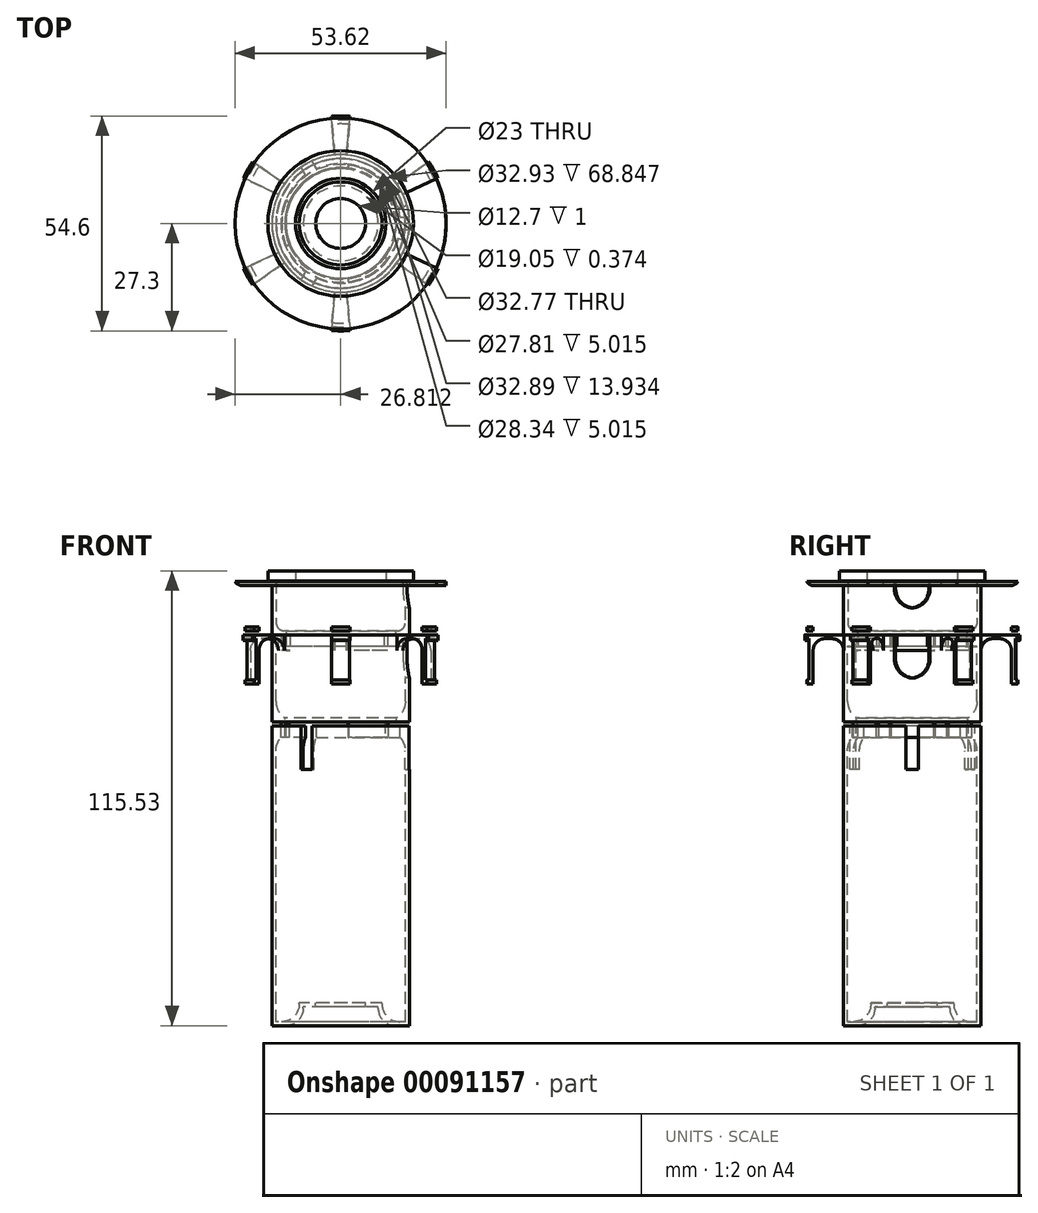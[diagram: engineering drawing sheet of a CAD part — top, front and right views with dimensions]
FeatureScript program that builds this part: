
annotation { "Feature Type Name" : "Feature", "Feature Type Description" : "" }
export const myFeature = defineFeature(function(context is Context, id is Id, definition is map)
    precondition{}
    {
        {
            var Q0;
            Q0=qCreatedBy(makeId("Front.planeOp"),FACE);
            var sketch = newSketch(context, id + "F0", { "sketchPlane" : qUnion([Q0])});
            skLineSegment(sketch, "E0", {"start": v(-75.46, 76.2) * mm, "end": v(-75.46, 0) * mm});
            skLineSegment(sketch, "E1", {"start": v(-75.46, 0) * mm, "end": v(-79, 0) * mm});
            skLineSegment(sketch, "E2", {"start": v(-83.4, 4.39) * mm, "end": v(-83.4, 4.76) * mm});
            skLineSegment(sketch, "E3", {"start": v(-83.4, 4.76) * mm, "end": v(-92.92, 4.76) * mm});
            skLineSegment(sketch, "E4.0", {"start": v(-82.4, 5.76) * mm, "end": v(-92.92, 5.76) * mm});
            skLineSegment(sketch, "E4.1", {"start": v(-82.4, 5.49) * mm, "end": v(-82.4, 5.76) * mm});
            skLineSegment(sketch, "E4.2", {"start": v(-76.46, 1) * mm, "end": v(-77.9, 1) * mm});
            skLineSegment(sketch, "E4.3", {"start": v(-76.46, 76.2) * mm, "end": v(-76.46, 1) * mm});
            skLineSegment(sketch, "E5", {"start": v(-76.46, 76.2) * mm, "end": v(-75.46, 76.2) * mm});
            skLineSegment(sketch, "E6", {"start": v(-92.92, 5.76) * mm, "end": v(-92.92, 4.76) * mm});
            skLineSegment(sketch, "E7.bottom", {"start": v(-86.57, 2.98) * mm, "end": v(-99.27, 2.98) * mm});
            skLineSegment(sketch, "E7.top", {"start": v(-86.57, 8.54) * mm, "end": v(-99.27, 8.54) * mm});
            skLineSegment(sketch, "E7.left", {"start": v(-86.57, 2.98) * mm, "end": v(-86.57, 8.54) * mm});
            skLineSegment(sketch, "E7.right", {"start": v(-99.27, 2.98) * mm, "end": v(-99.27, 8.54) * mm});
            skPoint(sketch, "E7.middle", {"position": v(-92.92, 5.76) * mm});
            skPoint(sketch, "E8.middle", {"position": v(-76.46, 76.2) * mm});
            skPoint(sketch, "E9.visualSharp", {"position": v(-82.4, 1) * mm});
            skArc(sketch, "E9.filletArc", {"start": v(-82.4, 5.49) * mm, "mid": v(-81.08, 2.31) * mm, "end": v(-77.9, 1) * mm});
            skPoint(sketch, "E10.visualSharp", {"position": v(-83.4, 0) * mm});
            skArc(sketch, "E10.filletArc", {"start": v(-83.4, 4.39) * mm, "mid": v(-82.1, 1.29) * mm, "end": v(-79, 0) * mm});
            skLineSegment(sketch, "E11", {"start": v(-92.92, 105.6) * mm, "end": v(-92.92, -5.85) * mm});
            skLineSegment(sketch, "E12.bottom", {"start": v(-77.75, 76.2) * mm, "end": v(-76.46, 76.2) * mm});
            skLineSegment(sketch, "E12.top", {"start": v(-77.75, 73.2) * mm, "end": v(-76.46, 73.2) * mm});
            skLineSegment(sketch, "E12.left", {"start": v(-77.75, 76.2) * mm, "end": v(-77.75, 73.2) * mm});
            skLineSegment(sketch, "E12.right", {"start": v(-76.46, 76.2) * mm, "end": v(-76.46, 73.2) * mm});
            skLineSegment(sketch, "E13", {"start": v(-75.46, 91.36) * mm, "end": v(-75.46, 98.33) * mm});
            skLineSegment(sketch, "E14", {"start": v(-75.46, 98.33) * mm, "end": v(-76.47, 98.33) * mm});
            skLineSegment(sketch, "E15", {"start": v(-76.47, 98.33) * mm, "end": v(-76.47, 78.2) * mm});
            skLineSegment(sketch, "E16", {"start": v(-76.47, 78.2) * mm, "end": v(-78.75, 78.2) * mm});
            skLineSegment(sketch, "E17", {"start": v(-78.75, 78.2) * mm, "end": v(-78.75, 73.19) * mm});
            skLineSegment(sketch, "E18", {"start": v(-78.75, 73.19) * mm, "end": v(-77.75, 73.2) * mm});
            skLineSegment(sketch, "E19", {"start": v(-77.75, 77.2) * mm, "end": v(-75.46, 77.2) * mm});
            skLineSegment(sketch, "E20", {"start": v(-75.46, 77.2) * mm, "end": v(-75.46, 91.36) * mm});
            skLineSegment(sketch, "E21", {"start": v(-77.75, 77.2) * mm, "end": v(-77.75, 73.2) * mm});
            skLineSegment(sketch, "E22.bottom", {"start": v(-77.75, 77.2) * mm, "end": v(-78.75, 77.2) * mm});
            skLineSegment(sketch, "E22.top", {"start": v(-77.75, 73.19) * mm, "end": v(-78.75, 73.19) * mm});
            skLineSegment(sketch, "E22.left", {"start": v(-77.75, 77.2) * mm, "end": v(-77.75, 73.19) * mm});
            skLineSegment(sketch, "E22.right", {"start": v(-78.75, 77.2) * mm, "end": v(-78.75, 73.19) * mm});
            skLineSegment(sketch, "E23.bottom", {"start": v(-76.47, 98.33) * mm, "end": v(-67.62, 98.33) * mm});
            skLineSegment(sketch, "E23.top", {"start": v(-76.47, 99.33) * mm, "end": v(-67.62, 99.33) * mm});
            skLineSegment(sketch, "E23.left", {"start": v(-76.47, 98.33) * mm, "end": v(-76.47, 99.33) * mm});
            skLineSegment(sketch, "E23.right", {"start": v(-67.62, 98.33) * mm, "end": v(-67.62, 99.33) * mm});
            skLineSegment(sketch, "E24.bottom", {"start": v(-67.62, 98.33) * mm, "end": v(-66.62, 98.33) * mm});
            skLineSegment(sketch, "E24.top", {"start": v(-67.62, 87.83) * mm, "end": v(-66.62, 87.83) * mm});
            skLineSegment(sketch, "E24.left", {"start": v(-67.62, 98.32) * mm, "end": v(-67.62, 87.83) * mm});
            skLineSegment(sketch, "E24.right", {"start": v(-66.62, 98.32) * mm, "end": v(-66.62, 87.83) * mm});
            skLineSegment(sketch, "E25.bottom", {"start": v(-67.62, 87.83) * mm, "end": v(-66.12, 87.83) * mm});
            skLineSegment(sketch, "E25.top", {"start": v(-67.62, 86.83) * mm, "end": v(-66.12, 86.83) * mm});
            skLineSegment(sketch, "E25.left", {"start": v(-67.62, 87.83) * mm, "end": v(-67.62, 86.83) * mm});
            skLineSegment(sketch, "E25.right", {"start": v(-66.12, 87.83) * mm, "end": v(-66.12, 86.83) * mm});
            skLineSegment(sketch, "E26.bottom", {"start": v(-67.62, 98.33) * mm, "end": v(-66.12, 98.33) * mm});
            skLineSegment(sketch, "E26.top", {"start": v(-67.62, 99.33) * mm, "end": v(-66.12, 99.33) * mm});
            skLineSegment(sketch, "E26.left", {"start": v(-67.62, 98.32) * mm, "end": v(-67.62, 99.33) * mm});
            skLineSegment(sketch, "E26.right", {"start": v(-66.12, 98.32) * mm, "end": v(-66.12, 99.33) * mm});
            skLineSegment(sketch, "E27", {"start": v(-67.62, 93.08) * mm, "end": v(-66.62, 93.08) * mm});
            skLineSegment(sketch, "E28.bottom", {"start": v(-66.12, 99.33) * mm, "end": v(-65.62, 99.33) * mm});
            skLineSegment(sketch, "E28.top", {"start": v(-66.12, 97.83) * mm, "end": v(-65.62, 97.83) * mm});
            skLineSegment(sketch, "E28.left", {"start": v(-66.12, 99.33) * mm, "end": v(-66.12, 97.83) * mm});
            skLineSegment(sketch, "E28.right", {"start": v(-65.62, 99.33) * mm, "end": v(-65.62, 97.83) * mm});
            skLineSegment(sketch, "E29", {"start": v(-75.46, 98.33) * mm, "end": v(-75.46, 99.33) * mm});
            skLineSegment(sketch, "E30.bottom", {"start": v(-76.47, 99.33) * mm, "end": v(-77.96, 99.33) * mm});
            skLineSegment(sketch, "E30.top", {"start": v(-76.47, 96.33) * mm, "end": v(-77.96, 96.33) * mm});
            skLineSegment(sketch, "E30.left", {"start": v(-76.47, 99.33) * mm, "end": v(-76.47, 96.33) * mm});
            skLineSegment(sketch, "E30.right", {"start": v(-77.96, 99.33) * mm, "end": v(-77.96, 96.33) * mm});
            skLineSegment(sketch, "E31", {"start": v(-76.47, 88.26) * mm, "end": v(-75.46, 88.26) * mm});
            skLineSegment(sketch, "E32.bottom", {"start": v(-74.42, 99.33) * mm, "end": v(-73.22, 99.33) * mm});
            skPoint(sketch, "E33.endSnap0", {"position": v(-77.96, 97.83) * mm});
            skLineSegment(sketch, "E34.bottom", {"start": v(-54.82, 105.48) * mm, "end": v(-54.82, 105.48) * mm});
            skLineSegment(sketch, "E34.top", {"start": v(-54.82, 105.48) * mm, "end": v(-54.82, 105.48) * mm});
            skLineSegment(sketch, "E34.left", {"start": v(-54.82, 105.48) * mm, "end": v(-54.82, 105.48) * mm});
            skLineSegment(sketch, "E34.right", {"start": v(-54.82, 105.48) * mm, "end": v(-54.82, 105.48) * mm});
            skLineSegment(sketch, "E35", {"start": v(-75.46, 111.83) * mm, "end": v(-75.46, 112.83) * mm});
            skLineSegment(sketch, "E36", {"start": v(-76.53, 111.83) * mm, "end": v(-76.53, 100.33) * mm});
            skLineSegment(sketch, "E37", {"start": v(-76.53, 100.33) * mm, "end": v(-79.01, 100.33) * mm});
            skLineSegment(sketch, "E38", {"start": v(-79.01, 100.33) * mm, "end": v(-79.01, 95.31) * mm});
            skLineSegment(sketch, "E39", {"start": v(-78.02, 99.33) * mm, "end": v(-75.46, 99.33) * mm});
            skLineSegment(sketch, "E40", {"start": v(-75.46, 99.33) * mm, "end": v(-75.46, 112.83) * mm});
            skLineSegment(sketch, "E41.top", {"start": v(-77.96, 95.31) * mm, "end": v(-79.01, 95.31) * mm});
            skLineSegment(sketch, "E41.left", {"start": v(-77.96, 99.33) * mm, "end": v(-77.96, 95.31) * mm});
            skLineSegment(sketch, "E41.right", {"start": v(-79.01, 99.33) * mm, "end": v(-79.01, 95.31) * mm});
            skLineSegment(sketch, "E42.bottom", {"start": v(-67.62, 101.33) * mm, "end": v(-66.12, 101.33) * mm});
            skLineSegment(sketch, "E42.top", {"start": v(-67.62, 100.33) * mm, "end": v(-66.12, 100.33) * mm});
            skLineSegment(sketch, "E42.left", {"start": v(-67.62, 101.33) * mm, "end": v(-67.62, 100.33) * mm});
            skLineSegment(sketch, "E42.right", {"start": v(-66.12, 101.33) * mm, "end": v(-66.12, 100.33) * mm});
            skLineSegment(sketch, "E43", {"start": v(-76.53, 111.83) * mm, "end": v(-67.62, 111.83) * mm});
            skLineSegment(sketch, "E44", {"start": v(-92.92, 105.6) * mm, "end": v(-92.92, 126.08) * mm});
            skLineSegment(sketch, "E45.bottom", {"start": v(-76.53, 111.83) * mm, "end": v(-66.1, 111.83) * mm});
            skLineSegment(sketch, "E45.top", {"start": v(-76.53, 112.83) * mm, "end": v(-66.1, 112.83) * mm});
            skLineSegment(sketch, "E45.left", {"start": v(-76.53, 111.83) * mm, "end": v(-76.53, 112.83) * mm});
            skLineSegment(sketch, "E45.right", {"start": v(-66.1, 111.83) * mm, "end": v(-66.1, 112.83) * mm});
            skLineSegment(sketch, "E46.bottom", {"start": v(-67.62, 111.83) * mm, "end": v(-66.62, 111.83) * mm});
            skLineSegment(sketch, "E46.top", {"start": v(-67.62, 101.33) * mm, "end": v(-66.62, 101.33) * mm});
            skLineSegment(sketch, "E46.left", {"start": v(-67.62, 111.83) * mm, "end": v(-67.62, 101.33) * mm});
            skLineSegment(sketch, "E46.right", {"start": v(-66.62, 111.83) * mm, "end": v(-66.62, 101.33) * mm});
            skLineSegment(sketch, "E47", {"start": v(-79.01, 99.33) * mm, "end": v(-77.96, 99.33) * mm});
            skLineSegment(sketch, "E48.bottom", {"start": v(-81.42, 113.03) * mm, "end": v(-74.42, 113.03) * mm});
            skLineSegment(sketch, "E48.top", {"start": v(-81.42, 115.53) * mm, "end": v(-74.42, 115.53) * mm});
            skLineSegment(sketch, "E48.left", {"start": v(-81.42, 113.03) * mm, "end": v(-81.42, 115.53) * mm});
            skLineSegment(sketch, "E48.right", {"start": v(-74.42, 113.03) * mm, "end": v(-74.42, 115.53) * mm});
            skLineSegment(sketch, "E49", {"start": v(-92.92, 121.65) * mm, "end": v(-56.65, 121.65) * mm});
            skLineSegment(sketch, "E50", {"start": v(-76.53, 106.08) * mm, "end": v(-75.46, 106.08) * mm});
            skSolve(sketch);
        }
        {
            var Q0;
            Q0=makeQuery(id+"F0.imprint","IMPRINT",FACE,{"disambiguationData":[TD([[makeQuery(id+"F0.imprint","IMPRINT",EDGE,{"derivedFrom":sQuery(id+"F0.wireOp",EDGE,"E0")}),-1.0]])]});
            var Q1;
            {var subQ5=sQuery(id+"F0.wireOp",EDGE,"E1");Q1=makeQuery(id+"F0.imprint","IMPRINT",FACE,{"disambiguationData":[TD([[makeQuery(id+"F0.imprint","IMPRINT",EDGE,{"derivedFrom":subQ5}),-1.0]])]});}
            var Q2;
            Q2=makeQuery(id+"F0.imprint","IMPRINT",FACE,{"disambiguationData":[TD([[makeQuery(id+"F0.imprint","IMPRINT",EDGE,{"derivedFrom":sQuery(id+"F0.wireOp",EDGE,"E12.bottom")}),-1.0]])]});
            var Q3;
            Q3=sQuery(id+"F0.wireOp",EDGE,"E6");
            revolve(context, id + "F1", {"entities" : qUnion([Q0, Q1, Q2]), "axis" : qUnion([Q3]), "revolveType" : RevolveType.FULL});
        }
        {
            var Q0;
            Q0=sQuery(id+"F0.wireOp",EDGE,"E1");
            var Q1;
            Q1=sQuery(id+"F0.wireOp",VERTEX,"E1.start");
            cPlane(context, id + "F2", {"entities" : qUnion([Q0, Q1]), "cplaneType" : CPlaneType.LINE_POINT, "offset" : 150 * mm, "width" : 150 * mm, "height" : 150 * mm});
        }
        {
            var Q0;
            Q0=qCreatedBy(id+"F2.planeOp",FACE);
            var sketch = newSketch(context, id + "F3", { "sketchPlane" : qUnion([Q0])});
            skLineSegment(sketch, "E51.bottom", {"start": v(-1.59, 65.09) * mm, "end": v(1.59, 65.09) * mm});
            skLineSegment(sketch, "E51.top", {"start": v(-1.59, 76.2) * mm, "end": v(1.59, 76.2) * mm});
            skLineSegment(sketch, "E51.left", {"start": v(-1.59, 65.09) * mm, "end": v(-1.59, 76.2) * mm});
            skLineSegment(sketch, "E51.right", {"start": v(1.59, 65.09) * mm, "end": v(1.59, 76.2) * mm});
            skPoint(sketch, "E51.middle", {"position": v(0, 70.64) * mm});
            skLineSegment(sketch, "E52.bottom", {"start": v(-3.65, 76.3) * mm, "end": v(3.11, 76.3) * mm});
            skLineSegment(sketch, "E52.top", {"start": v(-3.65, 68.35) * mm, "end": v(3.11, 68.35) * mm});
            skLineSegment(sketch, "E52.left", {"start": v(-3.65, 76.3) * mm, "end": v(-3.65, 68.35) * mm});
            skLineSegment(sketch, "E52.right", {"start": v(3.11, 76.3) * mm, "end": v(3.11, 68.35) * mm});
            skSolve(sketch);
        }
        {
            var Q0;
            Q0=makeQuery(id+"F3.imprint","IMPRINT",FACE,{"disambiguationData":[TD([[makeQuery(id+"F3.imprint","IMPRINT",EDGE,{"derivedFrom":sQuery(id+"F3.wireOp",EDGE,"E51.bottom")}),1.0]])]});
            var Q1;
            {var subQ0=sQuery(id+"F3.wireOp",EDGE,"E51.top");Q1=makeQuery(id+"F3.imprint","IMPRINT",FACE,{"disambiguationData":[TD([[makeQuery(id+"F3.imprint","IMPRINT",EDGE,{"derivedFrom":subQ0}),-1.0]])]});}
            extrude(context, id + "F4", {"entities" : qUnion([Q0, Q1]), "endBound" : BoundingType.SYMMETRIC, "depth" : 10 * mm});
        }
        {
            var Q0;
            Q0=makeQuery(id+"F4.opExtrude","SWEPT_BODY",BODY,{"disambiguationData":[OSD([sQuery(id+"F3.wireOp",EDGE,"E51.bottom"),sQuery(id+"F3.wireOp",EDGE,"E51.top"),sQuery(id+"F3.wireOp",EDGE,"E51.left"),sQuery(id+"F3.wireOp",EDGE,"E51.right")])]});
            var Q1;
            Q1=sQuery(id+"F0.wireOp",EDGE,"E6");
            circularPattern(context, id + "F5", {"operationType" : NewBodyOperationType.REMOVE, "entities" : qUnion([Q0]), "axis" : qUnion([Q1]), "angle" : 120 * degree, "instanceCount" : 3});
        }
        {
            var Q0;
            {var subQ0=sQuery(id+"F0.wireOp",EDGE,"E4.3");var subQ1=sQuery(id+"F0.wireOp",EDGE,"E12.top");Q0=makeQuery(id+"F5.boolean.opBoolean","SPLIT",EDGE,{"disambiguationData":[TD([makeQuery(id+"F4.opExtrude","SWEPT_FACE",FACE,{"disambiguationData":[OSD([sQuery(id+"F3.wireOp",EDGE,"E51.left")])]})])],"derivedFrom":makeQuery(id+"F1.opRevolve","SWEPT_EDGE",EDGE,{"disambiguationData":[OSD([subQ0,subQ1,sQuery(id+"F0.wireOp",EDGE,"E12.right")])]})});}
            var Q1;
            {var subQ0=sQuery(id+"F0.wireOp",EDGE,"E4.3");var subQ1=sQuery(id+"F0.wireOp",EDGE,"E12.top");Q1=makeQuery(id+"F5.boolean.opBoolean","SPLIT",EDGE,{"disambiguationData":[TD([makeQuery(id+"F4.opExtrude","SWEPT_FACE",FACE,{"disambiguationData":[OSD([sQuery(id+"F3.wireOp",EDGE,"E51.right")])]})])],"derivedFrom":makeQuery(id+"F1.opRevolve","SWEPT_EDGE",EDGE,{"disambiguationData":[OSD([subQ0,subQ1,sQuery(id+"F0.wireOp",EDGE,"E12.right")])]})});}
            var Q2;
            {var subQ0=sQuery(id+"F0.wireOp",EDGE,"E4.3");var subQ1=sQuery(id+"F0.wireOp",EDGE,"E12.top");Q2=makeQuery(id+"F5.boolean.opBoolean","SPLIT",EDGE,{"disambiguationData":[TD([makeQuery(id+"F5.opPattern","COPY",FACE,{"derivedFrom":makeQuery(id+"F4.opExtrude","SWEPT_FACE",FACE,{"disambiguationData":[OSD([sQuery(id+"F3.wireOp",EDGE,"E51.right")])]}),"instanceName":"1"})])],"derivedFrom":makeQuery(id+"F1.opRevolve","SWEPT_EDGE",EDGE,{"disambiguationData":[OSD([subQ0,subQ1,sQuery(id+"F0.wireOp",EDGE,"E12.right")])]})});}
            fillet(context, id + "F6", {"entities" : qUnion([Q0, Q1, Q2]), "radius" : 5 * mm, "tangentPropagation" : true, "allowEdgeOverflow" : false});
        }
        {
            var Q0;
            Q0=makeQuery(id+"F0.imprint","IMPRINT",FACE,{"disambiguationData":[TD([[makeQuery(id+"F0.imprint","IMPRINT",EDGE,{"derivedFrom":sQuery(id+"F0.wireOp",EDGE,"E13")}),1.0]])]});
            var Q1;
            {var subQ3=sQuery(id+"F0.wireOp",EDGE,"E18");Q1=makeQuery(id+"F0.imprint","IMPRINT",FACE,{"disambiguationData":[TD([[makeQuery(id+"F0.imprint","IMPRINT",EDGE,{"derivedFrom":subQ3}),1.0]])]});}
            var Q2;
            Q2=makeQuery(id+"F0.imprint","IMPRINT",FACE,{"disambiguationData":[TD([[makeQuery(id+"F0.imprint","IMPRINT",EDGE,{"derivedFrom":sQuery(id+"F0.wireOp",EDGE,"E23.top")}),-1.0]])]});
            var Q3;
            {var subQ1=sQuery(id+"F0.wireOp",EDGE,"E26.top");Q3=makeQuery(id+"F0.imprint","IMPRINT",FACE,{"disambiguationData":[TD([[makeQuery(id+"F0.imprint","IMPRINT",EDGE,{"derivedFrom":subQ1}),-1.0]])]});}
            var Q4;
            {var subQ3=sQuery(id+"F0.wireOp",EDGE,"E28.bottom");Q4=makeQuery(id+"F0.imprint","IMPRINT",FACE,{"disambiguationData":[TD([[makeQuery(id+"F0.imprint","IMPRINT",EDGE,{"derivedFrom":subQ3}),-1.0]])]});}
            var Q5;
            {var subQ3=sQuery(id+"F0.wireOp",EDGE,"E27");Q5=makeQuery(id+"F0.imprint","IMPRINT",FACE,{"disambiguationData":[TD([[makeQuery(id+"F0.imprint","IMPRINT",EDGE,{"derivedFrom":subQ3}),1.0]])]});}
            var Q6;
            {var subQ3=sQuery(id+"F0.wireOp",EDGE,"E27");Q6=makeQuery(id+"F0.imprint","IMPRINT",FACE,{"disambiguationData":[TD([[makeQuery(id+"F0.imprint","IMPRINT",EDGE,{"derivedFrom":subQ3}),-1.0]])]});}
            var Q7;
            Q7=makeQuery(id+"F0.imprint","IMPRINT",FACE,{"disambiguationData":[TD([[makeQuery(id+"F0.imprint","IMPRINT",EDGE,{"derivedFrom":sQuery(id+"F0.wireOp",EDGE,"E25.top")}),1.0]])]});
            var Q8;
            {var subQ3=sQuery(id+"F0.wireOp",EDGE,"E30.bottom");Q8=makeQuery(id+"F0.imprint","IMPRINT",FACE,{"disambiguationData":[TD([[makeQuery(id+"F0.imprint","IMPRINT",EDGE,{"derivedFrom":subQ3}),1.0]])]});}
            var Q9;
            {var subQ1=sQuery(id+"F0.wireOp",EDGE,"E16");Q9=makeQuery(id+"F0.imprint","IMPRINT",FACE,{"disambiguationData":[TD([[makeQuery(id+"F0.imprint","IMPRINT",EDGE,{"derivedFrom":subQ1}),1.0]])]});}
            var Q10;
            {var subQ0=sQuery(id+"F0.wireOp",EDGE,"E29");Q10=makeQuery(id+"F0.imprint","IMPRINT",FACE,{"disambiguationData":[TD([[makeQuery(id+"F0.imprint","IMPRINT",EDGE,{"derivedFrom":subQ0}),1.0]])]});}
            var Q11;
            Q11=makeQuery(id+"F0.imprint","IMPRINT",FACE,{"disambiguationData":[TD([[makeQuery(id+"F0.imprint","IMPRINT",EDGE,{"derivedFrom":sQuery(id+"F0.wireOp",EDGE,"E32.bottom")}),1.0]])]});
            var Q12;
            Q12=sQuery(id+"F0.wireOp",EDGE,"E11");
            revolve(context, id + "F7", {"entities" : qUnion([Q0, Q1, Q2, Q3, Q4, Q5, Q6, Q7, Q8, Q9, Q10, Q11]), "axis" : qUnion([Q12]), "revolveType" : RevolveType.FULL});
        }
        {
            var Q0;
            {var subQ3=sQuery(id+"F0.wireOp",EDGE,"E18");Q0=makeQuery(id+"F0.imprint","IMPRINT",FACE,{"disambiguationData":[TD([[makeQuery(id+"F0.imprint","IMPRINT",EDGE,{"derivedFrom":subQ3}),1.0]])]});}
            var Q1;
            Q1=sQuery(id+"F0.wireOp",EDGE,"E11");
            revolve(context, id + "F8", {"entities" : qUnion([Q0]), "axis" : qUnion([Q1]), "revolveType" : RevolveType.SYMMETRIC, "angle" : 75 * degree});
        }
        {
            var Q0;
            Q0=makeQuery(id+"F8.opRevolve","SWEPT_BODY",BODY,{"disambiguationData":[OSD([sQuery(id+"F0.wireOp",EDGE,"E18"),sQuery(id+"F0.wireOp",EDGE,"E22.bottom"),sQuery(id+"F0.wireOp",EDGE,"E22.left"),sQuery(id+"F0.wireOp",EDGE,"E22.right")])]});
            var Q1;
            Q1=sQuery(id+"F0.wireOp",EDGE,"E11");
            circularPattern(context, id + "F9", {"operationType" : NewBodyOperationType.REMOVE, "entities" : qUnion([Q0]), "axis" : qUnion([Q1]), "angle" : 120 * degree, "instanceCount" : 3});
        }
        {
            var Q0;
            Q0=makeQuery(id+"F7.opRevolve","SWEPT_EDGE",EDGE,{"disambiguationData":[OSD([sQuery(id+"F0.wireOp",EDGE,"E15"),sQuery(id+"F0.wireOp",EDGE,"E16")])]});
            fillet(context, id + "F10", {"entities" : qUnion([Q0]), "radius" : 5 * mm, "tangentPropagation" : true, "allowEdgeOverflow" : false});
        }
        {
            var Q0;
            {var subQ2=sQuery(id+"F0.wireOp",EDGE,"E26.left");Q0=makeQuery(id+"F0.imprint","IMPRINT",FACE,{"disambiguationData":[TD([[makeQuery(id+"F0.imprint","IMPRINT",EDGE,{"derivedFrom":subQ2}),1.0]])]});}
            var Q1;
            {var subQ1=sQuery(id+"F0.wireOp",EDGE,"E26.top");Q1=makeQuery(id+"F0.imprint","IMPRINT",FACE,{"disambiguationData":[TD([[makeQuery(id+"F0.imprint","IMPRINT",EDGE,{"derivedFrom":subQ1}),-1.0]])]});}
            var Q2;
            {var subQ3=sQuery(id+"F0.wireOp",EDGE,"E28.bottom");Q2=makeQuery(id+"F0.imprint","IMPRINT",FACE,{"disambiguationData":[TD([[makeQuery(id+"F0.imprint","IMPRINT",EDGE,{"derivedFrom":subQ3}),-1.0]])]});}
            var Q3;
            {var subQ3=sQuery(id+"F0.wireOp",EDGE,"E27");Q3=makeQuery(id+"F0.imprint","IMPRINT",FACE,{"disambiguationData":[TD([[makeQuery(id+"F0.imprint","IMPRINT",EDGE,{"derivedFrom":subQ3}),1.0]])]});}
            var Q4;
            {var subQ3=sQuery(id+"F0.wireOp",EDGE,"E27");Q4=makeQuery(id+"F0.imprint","IMPRINT",FACE,{"disambiguationData":[TD([[makeQuery(id+"F0.imprint","IMPRINT",EDGE,{"derivedFrom":subQ3}),-1.0]])]});}
            var Q5;
            Q5=makeQuery(id+"F0.imprint","IMPRINT",FACE,{"disambiguationData":[TD([[makeQuery(id+"F0.imprint","IMPRINT",EDGE,{"derivedFrom":sQuery(id+"F0.wireOp",EDGE,"E25.top")}),1.0]])]});
            var Q6;
            Q6=makeQuery(id+"F0.imprint","IMPRINT",FACE,{"disambiguationData":[TD([[makeQuery(id+"F0.imprint","IMPRINT",EDGE,{"derivedFrom":sQuery(id+"F0.wireOp",EDGE,"E32.bottom")}),1.0]])]});
            var Q7;
            Q7=sQuery(id+"F0.wireOp",EDGE,"E11");
            revolve(context, id + "F11", {"entities" : qUnion([Q0, Q1, Q2, Q3, Q4, Q5, Q6]), "axis" : qUnion([Q7]), "revolveType" : RevolveType.SYMMETRIC, "angle" : 50 * degree});
        }
        {
            var Q0;
            Q0=makeQuery(id+"F11.opRevolve","SWEPT_BODY",BODY,{"disambiguationData":[OSD([sQuery(id+"F0.wireOp",EDGE,"E23.bottom"),sQuery(id+"F0.wireOp",EDGE,"E23.top"),sQuery(id+"F0.wireOp",EDGE,"E24.left"),sQuery(id+"F0.wireOp",EDGE,"E24.right"),sQuery(id+"F0.wireOp",EDGE,"E25.bottom"),sQuery(id+"F0.wireOp",EDGE,"E25.top"),sQuery(id+"F0.wireOp",EDGE,"E25.left"),sQuery(id+"F0.wireOp",EDGE,"E25.right"),sQuery(id+"F0.wireOp",EDGE,"E26.bottom"),sQuery(id+"F0.wireOp",EDGE,"E26.top"),sQuery(id+"F0.wireOp",EDGE,"E28.bottom"),sQuery(id+"F0.wireOp",EDGE,"E28.top"),sQuery(id+"F0.wireOp",EDGE,"E28.left"),sQuery(id+"F0.wireOp",EDGE,"E28.right"),sQuery(id+"F0.wireOp",EDGE,"E29")])]});
            var Q1;
            Q1=sQuery(id+"F0.wireOp",EDGE,"E11");
            circularPattern(context, id + "F12", {"operationType" : NewBodyOperationType.REMOVE, "entities" : qUnion([Q0]), "axis" : qUnion([Q1]), "angle" : 60 * degree, "instanceCount" : 6});
        }
        {
            var Q0;
            {var subQ1=sQuery(id+"F0.wireOp",EDGE,"E13");Q0=makeQuery(id+"F0.imprint","IMPRINT",FACE,{"disambiguationData":[TD([[makeQuery(id+"F0.imprint","IMPRINT",EDGE,{"derivedFrom":subQ1}),1.0]])]});}
            var Q1;
            {var subQ3=sQuery(id+"F0.wireOp",EDGE,"E30.bottom");Q1=makeQuery(id+"F0.imprint","IMPRINT",FACE,{"disambiguationData":[TD([[makeQuery(id+"F0.imprint","IMPRINT",EDGE,{"derivedFrom":subQ3}),1.0]])]});}
            var Q2;
            {var subQ0=sQuery(id+"F0.wireOp",EDGE,"E29");Q2=makeQuery(id+"F0.imprint","IMPRINT",FACE,{"disambiguationData":[TD([[makeQuery(id+"F0.imprint","IMPRINT",EDGE,{"derivedFrom":subQ0}),1.0]])]});}
            var Q3;
            Q3=sQuery(id+"F0.wireOp",EDGE,"E11");
            revolve(context, id + "F13", {"operationType" : NewBodyOperationType.REMOVE, "entities" : qUnion([Q0, Q1, Q2]), "axis" : qUnion([Q3]), "revolveType" : RevolveType.SYMMETRIC, "oppositeDirection" : true, "angle" : 30 * degree});
        }
        {
            var Q0;
            Q0=makeQuery(id+"F13.boolean.opBoolean","COPY",EDGE,{"derivedFrom":makeQuery(id+"F13.opRevolve","CAP_EDGE",EDGE,{"disambiguationData":[OSD([sQuery(id+"F0.wireOp",EDGE,"E31")])],"isStart":false})});
            var Q1;
            Q1=makeQuery(id+"F13.boolean.opBoolean","COPY",EDGE,{"derivedFrom":makeQuery(id+"F13.opRevolve","CAP_EDGE",EDGE,{"disambiguationData":[OSD([sQuery(id+"F0.wireOp",EDGE,"E31")])],"isStart":true})});
            fillet(context, id + "F14", {"entities" : qUnion([Q0, Q1]), "radius" : 5 * mm, "tangentPropagation" : true, "allowEdgeOverflow" : false});
        }
        {
            var Q0;
            Q0=makeQuery(id+"F13.boolean.opBoolean","SPLIT",EDGE,{"disambiguationData":[OD(1.0)],"derivedFrom":makeQuery(id+"F7.opRevolve","SWEPT_EDGE",EDGE,{"disambiguationData":[OSD([sQuery(id+"F0.wireOp",EDGE,"E13"),sQuery(id+"F0.wireOp",EDGE,"E23.bottom"),sQuery(id+"F0.wireOp",EDGE,"E29")])]})});
            var Q1;
            Q1=makeQuery(id+"F7.opRevolve","SWEPT_EDGE",EDGE,{"disambiguationData":[OSD([sQuery(id+"F0.wireOp",EDGE,"E23.bottom"),sQuery(id+"F0.wireOp",EDGE,"E24.left"),sQuery(id+"F0.wireOp",EDGE,"E26.bottom"),sQuery(id+"F0.wireOp",EDGE,"E26.left")])]});
            fillet(context, id + "F15", {"entities" : qUnion([Q0, Q1]), "radius" : 3 * mm, "tangentPropagation" : true, "allowEdgeOverflow" : false});
        }
        {
            var Q0;
            Q0=makeQuery(id+"F0.imprint","IMPRINT",FACE,{"disambiguationData":[TD([[makeQuery(id+"F0.imprint","IMPRINT",EDGE,{"derivedFrom":sQuery(id+"F0.wireOp",EDGE,"E42.bottom")}),-1.0]])]});
            var Q1;
            Q1=makeQuery(id+"F0.imprint","IMPRINT",FACE,{"disambiguationData":[TD([[makeQuery(id+"F0.imprint","IMPRINT",EDGE,{"derivedFrom":sQuery(id+"F0.wireOp",EDGE,"E46.bottom")}),-1.0]])]});
            var Q2;
            {var subQ3=sQuery(id+"F0.wireOp",EDGE,"E45.right");Q2=makeQuery(id+"F0.imprint","IMPRINT",FACE,{"disambiguationData":[TD([[makeQuery(id+"F0.imprint","IMPRINT",EDGE,{"derivedFrom":subQ3}),1.0]])]});}
            var Q3;
            {var subQ5=sQuery(id+"F0.wireOp",EDGE,"E45.left");Q3=makeQuery(id+"F0.imprint","IMPRINT",FACE,{"disambiguationData":[TD([[makeQuery(id+"F0.imprint","IMPRINT",EDGE,{"derivedFrom":subQ5}),-1.0]])]});}
            var Q4;
            {var subQ6=sQuery(id+"F0.wireOp",EDGE,"E36");Q4=makeQuery(id+"F0.imprint","IMPRINT",FACE,{"disambiguationData":[TD([[makeQuery(id+"F0.imprint","IMPRINT",EDGE,{"derivedFrom":subQ6}),1.0]])]});}
            var Q5;
            {var subQ3=sQuery(id+"F0.wireOp",EDGE,"E41.top");Q5=makeQuery(id+"F0.imprint","IMPRINT",FACE,{"disambiguationData":[TD([[makeQuery(id+"F0.imprint","IMPRINT",EDGE,{"derivedFrom":subQ3}),-1.0]])]});}
            var Q6;
            {var subQ7=sQuery(id+"F0.wireOp",EDGE,"E37");Q6=makeQuery(id+"F0.imprint","IMPRINT",FACE,{"disambiguationData":[TD([[makeQuery(id+"F0.imprint","IMPRINT",EDGE,{"derivedFrom":subQ7}),1.0]])]});}
            var Q7;
            Q7=sQuery(id+"F0.wireOp",EDGE,"E44");
            revolve(context, id + "F16", {"entities" : qUnion([Q0, Q1, Q2, Q3, Q4, Q5, Q6]), "axis" : qUnion([Q7]), "revolveType" : RevolveType.FULL});
        }
        {
            var Q0;
            {var subQ3=sQuery(id+"F0.wireOp",EDGE,"E41.top");Q0=makeQuery(id+"F0.imprint","IMPRINT",FACE,{"disambiguationData":[TD([[makeQuery(id+"F0.imprint","IMPRINT",EDGE,{"derivedFrom":subQ3}),-1.0]])]});}
            var Q1;
            Q1=sQuery(id+"F0.wireOp",EDGE,"E11");
            revolve(context, id + "F17", {"entities" : qUnion([Q0]), "axis" : qUnion([Q1]), "revolveType" : RevolveType.SYMMETRIC, "angle" : 75 * degree});
        }
        {
            var Q0;
            Q0=makeQuery(id+"F17.opRevolve","SWEPT_BODY",BODY,{"disambiguationData":[OSD([sQuery(id+"F0.wireOp",EDGE,"E41.top"),sQuery(id+"F0.wireOp",EDGE,"E41.left"),sQuery(id+"F0.wireOp",EDGE,"E41.right"),sQuery(id+"F0.wireOp",EDGE,"E47")])]});
            var Q1;
            Q1=sQuery(id+"F0.wireOp",EDGE,"E11");
            circularPattern(context, id + "F18", {"operationType" : NewBodyOperationType.REMOVE, "entities" : qUnion([Q0]), "axis" : qUnion([Q1]), "angle" : 120 * degree, "instanceCount" : 3});
        }
        {
            var Q0;
            Q0=makeQuery(id+"F16.opRevolve","SWEPT_EDGE",EDGE,{"disambiguationData":[OSD([sQuery(id+"F0.wireOp",EDGE,"E36"),sQuery(id+"F0.wireOp",EDGE,"E37")])]});
            fillet(context, id + "F19", {"entities" : qUnion([Q0]), "radius" : 2 * mm, "tangentPropagation" : true, "allowEdgeOverflow" : false});
        }
        {
            var Q0;
            Q0=makeQuery(id+"F0.imprint","IMPRINT",FACE,{"disambiguationData":[TD([[makeQuery(id+"F0.imprint","IMPRINT",EDGE,{"derivedFrom":sQuery(id+"F0.wireOp",EDGE,"E42.bottom")}),-1.0]])]});
            var Q1;
            Q1=makeQuery(id+"F0.imprint","IMPRINT",FACE,{"disambiguationData":[TD([[makeQuery(id+"F0.imprint","IMPRINT",EDGE,{"derivedFrom":sQuery(id+"F0.wireOp",EDGE,"E46.bottom")}),-1.0]])]});
            var Q2;
            {var subQ3=sQuery(id+"F0.wireOp",EDGE,"E45.right");Q2=makeQuery(id+"F0.imprint","IMPRINT",FACE,{"disambiguationData":[TD([[makeQuery(id+"F0.imprint","IMPRINT",EDGE,{"derivedFrom":subQ3}),1.0]])]});}
            var Q3;
            Q3=sQuery(id+"F0.wireOp",EDGE,"E44");
            revolve(context, id + "F20", {"entities" : qUnion([Q0, Q1, Q2]), "axis" : qUnion([Q3]), "revolveType" : RevolveType.SYMMETRIC, "angle" : 50 * degree});
        }
        {
            var Q0;
            Q0=makeQuery(id+"F20.opRevolve","SWEPT_BODY",BODY,{"disambiguationData":[OSD([sQuery(id+"F0.wireOp",EDGE,"E42.bottom"),sQuery(id+"F0.wireOp",EDGE,"E42.top"),sQuery(id+"F0.wireOp",EDGE,"E42.left"),sQuery(id+"F0.wireOp",EDGE,"E42.right"),sQuery(id+"F0.wireOp",EDGE,"E45.bottom"),sQuery(id+"F0.wireOp",EDGE,"E45.top"),sQuery(id+"F0.wireOp",EDGE,"E45.left"),sQuery(id+"F0.wireOp",EDGE,"E45.right"),sQuery(id+"F0.wireOp",EDGE,"E46.left"),sQuery(id+"F0.wireOp",EDGE,"E46.right")])]});
            var Q1;
            Q1=sQuery(id+"F0.wireOp",EDGE,"E44");
            circularPattern(context, id + "F21", {"operationType" : NewBodyOperationType.REMOVE, "entities" : qUnion([Q0]), "axis" : qUnion([Q1]), "angle" : 60 * degree, "instanceCount" : 6});
        }
        {
            var Q0;
            {var subQ0=sQuery(id+"F0.wireOp",EDGE,"E46.left");var subQ1=sQuery(id+"F0.wireOp",EDGE,"E45.bottom");var subQ2=sQuery(id+"F0.wireOp",EDGE,"E40");var subQ3=makeQuery(id+"F0.imprint","INTERSECT",VERTEX,{"derivedFrom":[subQ2,subQ1]});var subQ4=makeQuery(id+"F0.imprint","IMPRINT",EDGE,{"disambiguationData":[TD([[subQ3,-1.0]])],"derivedFrom":subQ1});var subQ5=sQuery(id+"F0.wireOp",EDGE,"E45.left");var subQ6=makeQuery(id+"F20.opRevolve","SWEPT_FACE",FACE,{"disambiguationData":[OSD([subQ1]),TDD([makeQuery(id+"F0.imprint","IMPRINT",EDGE,{"disambiguationData":[TD([[subQ3,1.0]])],"derivedFrom":subQ1}),subQ4])]});var subQ7=sQuery(id+"F0.wireOp",EDGE,"E46.right");var subQ8=sQuery(id+"F0.wireOp",EDGE,"E45.right");var subQ9=sQuery(id+"F0.wireOp",EDGE,"E45.top");var subQ10=sQuery(id+"F0.wireOp",EDGE,"E42.right");var subQ11=sQuery(id+"F0.wireOp",EDGE,"E42.left");var subQ12=sQuery(id+"F0.wireOp",EDGE,"E42.top");var subQ13=sQuery(id+"F0.wireOp",EDGE,"E42.bottom");Q0=makeQuery(id+"F21.boolean.opBoolean","SPLIT",EDGE,{"disambiguationData":[TD([makeQuery(id+"F16.opRevolve","SWEPT_FACE",FACE,{"disambiguationData":[OSD([subQ2])]}),makeQuery(id+"F16.opRevolve","SWEPT_FACE",FACE,{"disambiguationData":[OSD([subQ1]),TDD([subQ4])]}),makeQuery(id+"F21.opPattern","COPY",FACE,{"derivedFrom":makeQuery(id+"F20.opRevolve","CAP_FACE",FACE,{"disambiguationData":[OSD([subQ13,subQ12,subQ11,subQ10,subQ1,subQ9,subQ5,subQ8,subQ0,subQ7])],"isStart":false}),"instanceName":"3"}),makeQuery(id+"F21.opPattern","COPY",FACE,{"derivedFrom":subQ6,"instanceName":"3"}),makeQuery(id+"F21.opPattern","COPY",FACE,{"derivedFrom":makeQuery(id+"F20.opRevolve","CAP_FACE",FACE,{"disambiguationData":[OSD([subQ13,subQ12,subQ11,subQ10,subQ1,subQ9,subQ5,subQ8,subQ0,subQ7])],"isStart":true}),"instanceName":"4"}),makeQuery(id+"F21.opPattern","COPY",FACE,{"derivedFrom":subQ6,"instanceName":"4"})])],"derivedFrom":makeQuery(id+"F16.opRevolve","SWEPT_EDGE",EDGE,{"disambiguationData":[OSD([subQ2,subQ1])]})});}
            var Q1;
            {var subQ0=sQuery(id+"F0.wireOp",EDGE,"E46.left");var subQ1=sQuery(id+"F0.wireOp",EDGE,"E42.left");var subQ2=sQuery(id+"F0.wireOp",EDGE,"E46.bottom");var subQ3=sQuery(id+"F0.wireOp",EDGE,"E45.bottom");var subQ4=sQuery(id+"F0.wireOp",EDGE,"E46.right");var subQ5=sQuery(id+"F0.wireOp",EDGE,"E45.right");var subQ6=sQuery(id+"F0.wireOp",EDGE,"E45.left");var subQ7=sQuery(id+"F0.wireOp",EDGE,"E45.top");var subQ8=sQuery(id+"F0.wireOp",EDGE,"E42.right");var subQ9=sQuery(id+"F0.wireOp",EDGE,"E42.top");var subQ10=sQuery(id+"F0.wireOp",EDGE,"E42.bottom");Q1=makeQuery(id+"F21.boolean.opBoolean","SPLIT",EDGE,{"disambiguationData":[TD([makeQuery(id+"F21.opPattern","COPY",FACE,{"derivedFrom":makeQuery(id+"F20.opRevolve","CAP_FACE",FACE,{"disambiguationData":[OSD([subQ10,subQ9,subQ1,subQ8,subQ3,subQ7,subQ6,subQ5,subQ0,subQ4])],"isStart":false}),"instanceName":"4"})])],"derivedFrom":makeQuery(id+"F16.opRevolve","SWEPT_EDGE",EDGE,{"disambiguationData":[OSD([subQ3,subQ2,subQ0])]})});}
            var Q2;
            {var subQ0=sQuery(id+"F0.wireOp",EDGE,"E46.right");var subQ1=sQuery(id+"F0.wireOp",EDGE,"E46.left");var subQ2=sQuery(id+"F0.wireOp",EDGE,"E45.right");var subQ3=sQuery(id+"F0.wireOp",EDGE,"E45.left");var subQ4=sQuery(id+"F0.wireOp",EDGE,"E45.top");var subQ5=sQuery(id+"F0.wireOp",EDGE,"E45.bottom");var subQ6=sQuery(id+"F0.wireOp",EDGE,"E42.right");var subQ7=sQuery(id+"F0.wireOp",EDGE,"E42.left");var subQ8=sQuery(id+"F0.wireOp",EDGE,"E42.top");var subQ9=sQuery(id+"F0.wireOp",EDGE,"E42.bottom");var subQ10=sQuery(id+"F0.wireOp",EDGE,"E40");var subQ11=makeQuery(id+"F0.imprint","INTERSECT",VERTEX,{"derivedFrom":[subQ10,subQ5]});var subQ12=makeQuery(id+"F0.imprint","IMPRINT",EDGE,{"disambiguationData":[TD([[subQ11,-1.0]])],"derivedFrom":subQ5});var subQ13=makeQuery(id+"F20.opRevolve","SWEPT_FACE",FACE,{"disambiguationData":[OSD([subQ5]),TDD([makeQuery(id+"F0.imprint","IMPRINT",EDGE,{"disambiguationData":[TD([[subQ11,1.0]])],"derivedFrom":subQ5}),subQ12])]});Q2=makeQuery(id+"F21.boolean.opBoolean","SPLIT",EDGE,{"disambiguationData":[TD([makeQuery(id+"F16.opRevolve","SWEPT_FACE",FACE,{"disambiguationData":[OSD([subQ10])]}),makeQuery(id+"F16.opRevolve","SWEPT_FACE",FACE,{"disambiguationData":[OSD([subQ5]),TDD([subQ12])]}),makeQuery(id+"F21.opPattern","COPY",FACE,{"derivedFrom":makeQuery(id+"F20.opRevolve","CAP_FACE",FACE,{"disambiguationData":[OSD([subQ9,subQ8,subQ7,subQ6,subQ5,subQ4,subQ3,subQ2,subQ1,subQ0])],"isStart":false}),"instanceName":"2"}),makeQuery(id+"F21.opPattern","COPY",FACE,{"derivedFrom":subQ13,"instanceName":"2"}),makeQuery(id+"F21.opPattern","COPY",FACE,{"derivedFrom":makeQuery(id+"F20.opRevolve","CAP_FACE",FACE,{"disambiguationData":[OSD([subQ9,subQ8,subQ7,subQ6,subQ5,subQ4,subQ3,subQ2,subQ1,subQ0])],"isStart":true}),"instanceName":"3"}),makeQuery(id+"F21.opPattern","COPY",FACE,{"derivedFrom":subQ13,"instanceName":"3"})])],"derivedFrom":makeQuery(id+"F16.opRevolve","SWEPT_EDGE",EDGE,{"disambiguationData":[OSD([subQ10,subQ5])]})});}
            var Q3;
            {var subQ0=sQuery(id+"F0.wireOp",EDGE,"E46.left");var subQ1=sQuery(id+"F0.wireOp",EDGE,"E42.left");var subQ2=sQuery(id+"F0.wireOp",EDGE,"E46.bottom");var subQ3=sQuery(id+"F0.wireOp",EDGE,"E45.bottom");var subQ4=sQuery(id+"F0.wireOp",EDGE,"E46.right");var subQ5=sQuery(id+"F0.wireOp",EDGE,"E45.right");var subQ6=sQuery(id+"F0.wireOp",EDGE,"E45.left");var subQ7=sQuery(id+"F0.wireOp",EDGE,"E45.top");var subQ8=sQuery(id+"F0.wireOp",EDGE,"E42.right");var subQ9=sQuery(id+"F0.wireOp",EDGE,"E42.top");var subQ10=sQuery(id+"F0.wireOp",EDGE,"E42.bottom");Q3=makeQuery(id+"F21.boolean.opBoolean","SPLIT",EDGE,{"disambiguationData":[TD([makeQuery(id+"F21.opPattern","COPY",FACE,{"derivedFrom":makeQuery(id+"F20.opRevolve","CAP_FACE",FACE,{"disambiguationData":[OSD([subQ10,subQ9,subQ1,subQ8,subQ3,subQ7,subQ6,subQ5,subQ0,subQ4])],"isStart":false}),"instanceName":"3"})])],"derivedFrom":makeQuery(id+"F16.opRevolve","SWEPT_EDGE",EDGE,{"disambiguationData":[OSD([subQ3,subQ2,subQ0])]})});}
            var Q4;
            {var subQ0=sQuery(id+"F0.wireOp",EDGE,"E46.left");var subQ1=sQuery(id+"F0.wireOp",EDGE,"E42.left");var subQ2=sQuery(id+"F0.wireOp",EDGE,"E46.bottom");var subQ3=sQuery(id+"F0.wireOp",EDGE,"E45.bottom");var subQ4=sQuery(id+"F0.wireOp",EDGE,"E46.right");var subQ5=sQuery(id+"F0.wireOp",EDGE,"E45.right");var subQ6=sQuery(id+"F0.wireOp",EDGE,"E45.left");var subQ7=sQuery(id+"F0.wireOp",EDGE,"E45.top");var subQ8=sQuery(id+"F0.wireOp",EDGE,"E42.right");var subQ9=sQuery(id+"F0.wireOp",EDGE,"E42.top");var subQ10=sQuery(id+"F0.wireOp",EDGE,"E42.bottom");Q4=makeQuery(id+"F21.boolean.opBoolean","SPLIT",EDGE,{"disambiguationData":[TD([makeQuery(id+"F21.opPattern","COPY",FACE,{"derivedFrom":makeQuery(id+"F20.opRevolve","CAP_FACE",FACE,{"disambiguationData":[OSD([subQ10,subQ9,subQ1,subQ8,subQ3,subQ7,subQ6,subQ5,subQ0,subQ4])],"isStart":false}),"instanceName":"2"})])],"derivedFrom":makeQuery(id+"F16.opRevolve","SWEPT_EDGE",EDGE,{"disambiguationData":[OSD([subQ3,subQ2,subQ0])]})});}
            var Q5;
            {var subQ0=sQuery(id+"F0.wireOp",EDGE,"E46.left");var subQ1=sQuery(id+"F0.wireOp",EDGE,"E45.bottom");var subQ2=sQuery(id+"F0.wireOp",EDGE,"E40");var subQ3=makeQuery(id+"F0.imprint","INTERSECT",VERTEX,{"derivedFrom":[subQ2,subQ1]});var subQ4=makeQuery(id+"F0.imprint","IMPRINT",EDGE,{"disambiguationData":[TD([[subQ3,-1.0]])],"derivedFrom":subQ1});var subQ5=sQuery(id+"F0.wireOp",EDGE,"E45.left");var subQ6=makeQuery(id+"F20.opRevolve","SWEPT_FACE",FACE,{"disambiguationData":[OSD([subQ1]),TDD([makeQuery(id+"F0.imprint","IMPRINT",EDGE,{"disambiguationData":[TD([[subQ3,1.0]])],"derivedFrom":subQ1}),subQ4])]});var subQ7=sQuery(id+"F0.wireOp",EDGE,"E46.right");var subQ8=sQuery(id+"F0.wireOp",EDGE,"E45.right");var subQ9=sQuery(id+"F0.wireOp",EDGE,"E45.top");var subQ10=sQuery(id+"F0.wireOp",EDGE,"E42.right");var subQ11=sQuery(id+"F0.wireOp",EDGE,"E42.left");var subQ12=sQuery(id+"F0.wireOp",EDGE,"E42.top");var subQ13=sQuery(id+"F0.wireOp",EDGE,"E42.bottom");Q5=makeQuery(id+"F21.boolean.opBoolean","SPLIT",EDGE,{"disambiguationData":[TD([makeQuery(id+"F16.opRevolve","SWEPT_FACE",FACE,{"disambiguationData":[OSD([subQ2])]}),makeQuery(id+"F16.opRevolve","SWEPT_FACE",FACE,{"disambiguationData":[OSD([subQ1]),TDD([subQ4])]}),makeQuery(id+"F20.opRevolve","CAP_FACE",FACE,{"disambiguationData":[OSD([subQ13,subQ12,subQ11,subQ10,subQ1,subQ9,subQ5,subQ8,subQ0,subQ7])],"isStart":true}),subQ6,makeQuery(id+"F21.opPattern","COPY",FACE,{"derivedFrom":makeQuery(id+"F20.opRevolve","CAP_FACE",FACE,{"disambiguationData":[OSD([subQ13,subQ12,subQ11,subQ10,subQ1,subQ9,subQ5,subQ8,subQ0,subQ7])],"isStart":false}),"instanceName":"5"}),makeQuery(id+"F21.opPattern","COPY",FACE,{"derivedFrom":subQ6,"instanceName":"5"})])],"derivedFrom":makeQuery(id+"F16.opRevolve","SWEPT_EDGE",EDGE,{"disambiguationData":[OSD([subQ2,subQ1])]})});}
            var Q6;
            {var subQ0=sQuery(id+"F0.wireOp",EDGE,"E46.left");var subQ1=sQuery(id+"F0.wireOp",EDGE,"E45.bottom");var subQ2=sQuery(id+"F0.wireOp",EDGE,"E40");var subQ3=makeQuery(id+"F0.imprint","INTERSECT",VERTEX,{"derivedFrom":[subQ2,subQ1]});var subQ4=makeQuery(id+"F0.imprint","IMPRINT",EDGE,{"disambiguationData":[TD([[subQ3,-1.0]])],"derivedFrom":subQ1});var subQ5=sQuery(id+"F0.wireOp",EDGE,"E45.left");var subQ6=makeQuery(id+"F20.opRevolve","SWEPT_FACE",FACE,{"disambiguationData":[OSD([subQ1]),TDD([makeQuery(id+"F0.imprint","IMPRINT",EDGE,{"disambiguationData":[TD([[subQ3,1.0]])],"derivedFrom":subQ1}),subQ4])]});var subQ7=sQuery(id+"F0.wireOp",EDGE,"E46.right");var subQ8=sQuery(id+"F0.wireOp",EDGE,"E45.right");var subQ9=sQuery(id+"F0.wireOp",EDGE,"E45.top");var subQ10=sQuery(id+"F0.wireOp",EDGE,"E42.right");var subQ11=sQuery(id+"F0.wireOp",EDGE,"E42.left");var subQ12=sQuery(id+"F0.wireOp",EDGE,"E42.top");var subQ13=sQuery(id+"F0.wireOp",EDGE,"E42.bottom");Q6=makeQuery(id+"F21.boolean.opBoolean","SPLIT",EDGE,{"disambiguationData":[TD([makeQuery(id+"F16.opRevolve","SWEPT_FACE",FACE,{"disambiguationData":[OSD([subQ2])]}),makeQuery(id+"F16.opRevolve","SWEPT_FACE",FACE,{"disambiguationData":[OSD([subQ1]),TDD([subQ4])]}),makeQuery(id+"F21.opPattern","COPY",FACE,{"derivedFrom":makeQuery(id+"F20.opRevolve","CAP_FACE",FACE,{"disambiguationData":[OSD([subQ13,subQ12,subQ11,subQ10,subQ1,subQ9,subQ5,subQ8,subQ0,subQ7])],"isStart":false}),"instanceName":"1"}),makeQuery(id+"F21.opPattern","COPY",FACE,{"derivedFrom":subQ6,"instanceName":"1"}),makeQuery(id+"F21.opPattern","COPY",FACE,{"derivedFrom":makeQuery(id+"F20.opRevolve","CAP_FACE",FACE,{"disambiguationData":[OSD([subQ13,subQ12,subQ11,subQ10,subQ1,subQ9,subQ5,subQ8,subQ0,subQ7])],"isStart":true}),"instanceName":"2"}),makeQuery(id+"F21.opPattern","COPY",FACE,{"derivedFrom":subQ6,"instanceName":"2"})])],"derivedFrom":makeQuery(id+"F16.opRevolve","SWEPT_EDGE",EDGE,{"disambiguationData":[OSD([subQ2,subQ1])]})});}
            var Q7;
            {var subQ0=sQuery(id+"F0.wireOp",EDGE,"E46.left");var subQ1=sQuery(id+"F0.wireOp",EDGE,"E45.bottom");var subQ2=sQuery(id+"F0.wireOp",EDGE,"E40");var subQ3=makeQuery(id+"F0.imprint","INTERSECT",VERTEX,{"derivedFrom":[subQ2,subQ1]});var subQ4=makeQuery(id+"F0.imprint","IMPRINT",EDGE,{"disambiguationData":[TD([[subQ3,-1.0]])],"derivedFrom":subQ1});var subQ5=sQuery(id+"F0.wireOp",EDGE,"E45.left");var subQ6=makeQuery(id+"F20.opRevolve","SWEPT_FACE",FACE,{"disambiguationData":[OSD([subQ1]),TDD([makeQuery(id+"F0.imprint","IMPRINT",EDGE,{"disambiguationData":[TD([[subQ3,1.0]])],"derivedFrom":subQ1}),subQ4])]});var subQ7=sQuery(id+"F0.wireOp",EDGE,"E46.right");var subQ8=sQuery(id+"F0.wireOp",EDGE,"E45.right");var subQ9=sQuery(id+"F0.wireOp",EDGE,"E45.top");var subQ10=sQuery(id+"F0.wireOp",EDGE,"E42.right");var subQ11=sQuery(id+"F0.wireOp",EDGE,"E42.left");var subQ12=sQuery(id+"F0.wireOp",EDGE,"E42.top");var subQ13=sQuery(id+"F0.wireOp",EDGE,"E42.bottom");Q7=makeQuery(id+"F21.boolean.opBoolean","SPLIT",EDGE,{"disambiguationData":[TD([makeQuery(id+"F16.opRevolve","SWEPT_FACE",FACE,{"disambiguationData":[OSD([subQ2])]}),makeQuery(id+"F16.opRevolve","SWEPT_FACE",FACE,{"disambiguationData":[OSD([subQ1]),TDD([subQ4])]}),makeQuery(id+"F20.opRevolve","CAP_FACE",FACE,{"disambiguationData":[OSD([subQ13,subQ12,subQ11,subQ10,subQ1,subQ9,subQ5,subQ8,subQ0,subQ7])],"isStart":false}),subQ6,makeQuery(id+"F21.opPattern","COPY",FACE,{"derivedFrom":makeQuery(id+"F20.opRevolve","CAP_FACE",FACE,{"disambiguationData":[OSD([subQ13,subQ12,subQ11,subQ10,subQ1,subQ9,subQ5,subQ8,subQ0,subQ7])],"isStart":true}),"instanceName":"1"}),makeQuery(id+"F21.opPattern","COPY",FACE,{"derivedFrom":subQ6,"instanceName":"1"})])],"derivedFrom":makeQuery(id+"F16.opRevolve","SWEPT_EDGE",EDGE,{"disambiguationData":[OSD([subQ2,subQ1])]})});}
            var Q8;
            {var subQ0=sQuery(id+"F0.wireOp",EDGE,"E46.left");var subQ1=sQuery(id+"F0.wireOp",EDGE,"E42.left");var subQ2=sQuery(id+"F0.wireOp",EDGE,"E46.bottom");var subQ3=sQuery(id+"F0.wireOp",EDGE,"E45.bottom");var subQ4=sQuery(id+"F0.wireOp",EDGE,"E46.right");var subQ5=sQuery(id+"F0.wireOp",EDGE,"E45.right");var subQ6=sQuery(id+"F0.wireOp",EDGE,"E45.left");var subQ7=sQuery(id+"F0.wireOp",EDGE,"E45.top");var subQ8=sQuery(id+"F0.wireOp",EDGE,"E42.right");var subQ9=sQuery(id+"F0.wireOp",EDGE,"E42.top");var subQ10=sQuery(id+"F0.wireOp",EDGE,"E42.bottom");Q8=makeQuery(id+"F21.boolean.opBoolean","SPLIT",EDGE,{"disambiguationData":[TD([makeQuery(id+"F20.opRevolve","CAP_FACE",FACE,{"disambiguationData":[OSD([subQ10,subQ9,subQ1,subQ8,subQ3,subQ7,subQ6,subQ5,subQ0,subQ4])],"isStart":true})])],"derivedFrom":makeQuery(id+"F16.opRevolve","SWEPT_EDGE",EDGE,{"disambiguationData":[OSD([subQ3,subQ2,subQ0])]})});}
            var Q9;
            {var subQ0=sQuery(id+"F0.wireOp",EDGE,"E46.left");var subQ1=sQuery(id+"F0.wireOp",EDGE,"E42.left");var subQ2=sQuery(id+"F0.wireOp",EDGE,"E46.bottom");var subQ3=sQuery(id+"F0.wireOp",EDGE,"E45.bottom");var subQ4=sQuery(id+"F0.wireOp",EDGE,"E46.right");var subQ5=sQuery(id+"F0.wireOp",EDGE,"E45.right");var subQ6=sQuery(id+"F0.wireOp",EDGE,"E45.left");var subQ7=sQuery(id+"F0.wireOp",EDGE,"E45.top");var subQ8=sQuery(id+"F0.wireOp",EDGE,"E42.right");var subQ9=sQuery(id+"F0.wireOp",EDGE,"E42.top");var subQ10=sQuery(id+"F0.wireOp",EDGE,"E42.bottom");Q9=makeQuery(id+"F21.boolean.opBoolean","SPLIT",EDGE,{"disambiguationData":[TD([makeQuery(id+"F20.opRevolve","CAP_FACE",FACE,{"disambiguationData":[OSD([subQ10,subQ9,subQ1,subQ8,subQ3,subQ7,subQ6,subQ5,subQ0,subQ4])],"isStart":false})])],"derivedFrom":makeQuery(id+"F16.opRevolve","SWEPT_EDGE",EDGE,{"disambiguationData":[OSD([subQ3,subQ2,subQ0])]})});}
            var Q10;
            {var subQ0=sQuery(id+"F0.wireOp",EDGE,"E46.left");var subQ1=sQuery(id+"F0.wireOp",EDGE,"E42.left");var subQ2=sQuery(id+"F0.wireOp",EDGE,"E46.bottom");var subQ3=sQuery(id+"F0.wireOp",EDGE,"E45.bottom");var subQ4=sQuery(id+"F0.wireOp",EDGE,"E46.right");var subQ5=sQuery(id+"F0.wireOp",EDGE,"E45.right");var subQ6=sQuery(id+"F0.wireOp",EDGE,"E45.left");var subQ7=sQuery(id+"F0.wireOp",EDGE,"E45.top");var subQ8=sQuery(id+"F0.wireOp",EDGE,"E42.right");var subQ9=sQuery(id+"F0.wireOp",EDGE,"E42.top");var subQ10=sQuery(id+"F0.wireOp",EDGE,"E42.bottom");Q10=makeQuery(id+"F21.boolean.opBoolean","SPLIT",EDGE,{"disambiguationData":[TD([makeQuery(id+"F21.opPattern","COPY",FACE,{"derivedFrom":makeQuery(id+"F20.opRevolve","CAP_FACE",FACE,{"disambiguationData":[OSD([subQ10,subQ9,subQ1,subQ8,subQ3,subQ7,subQ6,subQ5,subQ0,subQ4])],"isStart":false}),"instanceName":"1"})])],"derivedFrom":makeQuery(id+"F16.opRevolve","SWEPT_EDGE",EDGE,{"disambiguationData":[OSD([subQ3,subQ2,subQ0])]})});}
            var Q11;
            {var subQ0=sQuery(id+"F0.wireOp",EDGE,"E46.right");var subQ1=sQuery(id+"F0.wireOp",EDGE,"E46.left");var subQ2=sQuery(id+"F0.wireOp",EDGE,"E45.right");var subQ3=sQuery(id+"F0.wireOp",EDGE,"E45.left");var subQ4=sQuery(id+"F0.wireOp",EDGE,"E45.top");var subQ5=sQuery(id+"F0.wireOp",EDGE,"E45.bottom");var subQ6=sQuery(id+"F0.wireOp",EDGE,"E42.right");var subQ7=sQuery(id+"F0.wireOp",EDGE,"E42.left");var subQ8=sQuery(id+"F0.wireOp",EDGE,"E42.top");var subQ9=sQuery(id+"F0.wireOp",EDGE,"E42.bottom");var subQ10=sQuery(id+"F0.wireOp",EDGE,"E40");var subQ11=makeQuery(id+"F0.imprint","INTERSECT",VERTEX,{"derivedFrom":[subQ10,subQ5]});var subQ12=makeQuery(id+"F0.imprint","IMPRINT",EDGE,{"disambiguationData":[TD([[subQ11,-1.0]])],"derivedFrom":subQ5});var subQ13=makeQuery(id+"F20.opRevolve","SWEPT_FACE",FACE,{"disambiguationData":[OSD([subQ5]),TDD([makeQuery(id+"F0.imprint","IMPRINT",EDGE,{"disambiguationData":[TD([[subQ11,1.0]])],"derivedFrom":subQ5}),subQ12])]});Q11=makeQuery(id+"F21.boolean.opBoolean","SPLIT",EDGE,{"disambiguationData":[TD([makeQuery(id+"F16.opRevolve","SWEPT_FACE",FACE,{"disambiguationData":[OSD([subQ10])]}),makeQuery(id+"F16.opRevolve","SWEPT_FACE",FACE,{"disambiguationData":[OSD([subQ5]),TDD([subQ12])]}),makeQuery(id+"F21.opPattern","COPY",FACE,{"derivedFrom":makeQuery(id+"F20.opRevolve","CAP_FACE",FACE,{"disambiguationData":[OSD([subQ9,subQ8,subQ7,subQ6,subQ5,subQ4,subQ3,subQ2,subQ1,subQ0])],"isStart":false}),"instanceName":"4"}),makeQuery(id+"F21.opPattern","COPY",FACE,{"derivedFrom":subQ13,"instanceName":"4"}),makeQuery(id+"F21.opPattern","COPY",FACE,{"derivedFrom":makeQuery(id+"F20.opRevolve","CAP_FACE",FACE,{"disambiguationData":[OSD([subQ9,subQ8,subQ7,subQ6,subQ5,subQ4,subQ3,subQ2,subQ1,subQ0])],"isStart":true}),"instanceName":"5"}),makeQuery(id+"F21.opPattern","COPY",FACE,{"derivedFrom":subQ13,"instanceName":"5"})])],"derivedFrom":makeQuery(id+"F16.opRevolve","SWEPT_EDGE",EDGE,{"disambiguationData":[OSD([subQ10,subQ5])]})});}
            fillet(context, id + "F22", {"entities" : qUnion([Q0, Q1, Q2, Q3, Q4, Q5, Q6, Q7, Q8, Q9, Q10, Q11]), "radius" : 2 * mm, "tangentPropagation" : true, "allowEdgeOverflow" : false});
        }
        {
            var Q0;
            {var subQ3=sQuery(id+"F0.wireOp",EDGE,"E50");Q0=makeQuery(id+"F0.imprint","IMPRINT",FACE,{"disambiguationData":[TD([[makeQuery(id+"F0.imprint","IMPRINT",EDGE,{"derivedFrom":subQ3}),1.0]])]});}
            var Q1;
            {var subQ5=sQuery(id+"F0.wireOp",EDGE,"E45.left");Q1=makeQuery(id+"F0.imprint","IMPRINT",FACE,{"disambiguationData":[TD([[makeQuery(id+"F0.imprint","IMPRINT",EDGE,{"derivedFrom":subQ5}),-1.0]])]});}
            var Q2;
            {var subQ0=sQuery(id+"F0.wireOp",EDGE,"E40");var subQ1=makeQuery(id+"F20.opRevolve","SWEPT_FACE",FACE,{"disambiguationData":[OSD([subQ0])]});Q2=makeQuery(id+"F21.boolean.opBoolean","MERGE",FACE,{"derivedFrom":[makeQuery(id+"F16.opRevolve","SWEPT_FACE",FACE,{"disambiguationData":[OSD([subQ0])]}),subQ1,makeQuery(id+"F21.opPattern","COPY",FACE,{"derivedFrom":subQ1,"instanceName":"1"}),makeQuery(id+"F21.opPattern","COPY",FACE,{"derivedFrom":subQ1,"instanceName":"2"}),makeQuery(id+"F21.opPattern","COPY",FACE,{"derivedFrom":subQ1,"instanceName":"3"}),makeQuery(id+"F21.opPattern","COPY",FACE,{"derivedFrom":subQ1,"instanceName":"4"}),makeQuery(id+"F21.opPattern","COPY",FACE,{"derivedFrom":subQ1,"instanceName":"5"})]});}
            revolve(context, id + "F23", {"operationType" : NewBodyOperationType.REMOVE, "entities" : qUnion([Q0, Q1]), "axis" : qUnion([Q2]), "revolveType" : RevolveType.SYMMETRIC, "oppositeDirection" : true, "angle" : 30 * degree});
        }
        {
            var Q0;
            Q0=makeQuery(id+"F23.boolean.opBoolean","COPY",EDGE,{"derivedFrom":makeQuery(id+"F23.opRevolve","CAP_EDGE",EDGE,{"disambiguationData":[OSD([sQuery(id+"F0.wireOp",EDGE,"E50")])],"isStart":false})});
            var Q1;
            Q1=makeQuery(id+"F23.boolean.opBoolean","COPY",EDGE,{"derivedFrom":makeQuery(id+"F23.opRevolve","CAP_EDGE",EDGE,{"disambiguationData":[OSD([sQuery(id+"F0.wireOp",EDGE,"E50")])],"isStart":true})});
            fillet(context, id + "F24", {"entities" : qUnion([Q0, Q1]), "radius" : 5 * mm, "tangentPropagation" : true, "allowEdgeOverflow" : false});
        }
        {
            var Q0;
            Q0=makeQuery(id+"F0.imprint","IMPRINT",FACE,{"disambiguationData":[TD([[makeQuery(id+"F0.imprint","IMPRINT",EDGE,{"derivedFrom":sQuery(id+"F0.wireOp",EDGE,"E48.bottom")}),1.0]])]});
            var Q1;
            Q1=sQuery(id+"F0.wireOp",EDGE,"E44");
            revolve(context, id + "F25", {"entities" : qUnion([Q0]), "axis" : qUnion([Q1]), "revolveType" : RevolveType.FULL});
        }
    });
